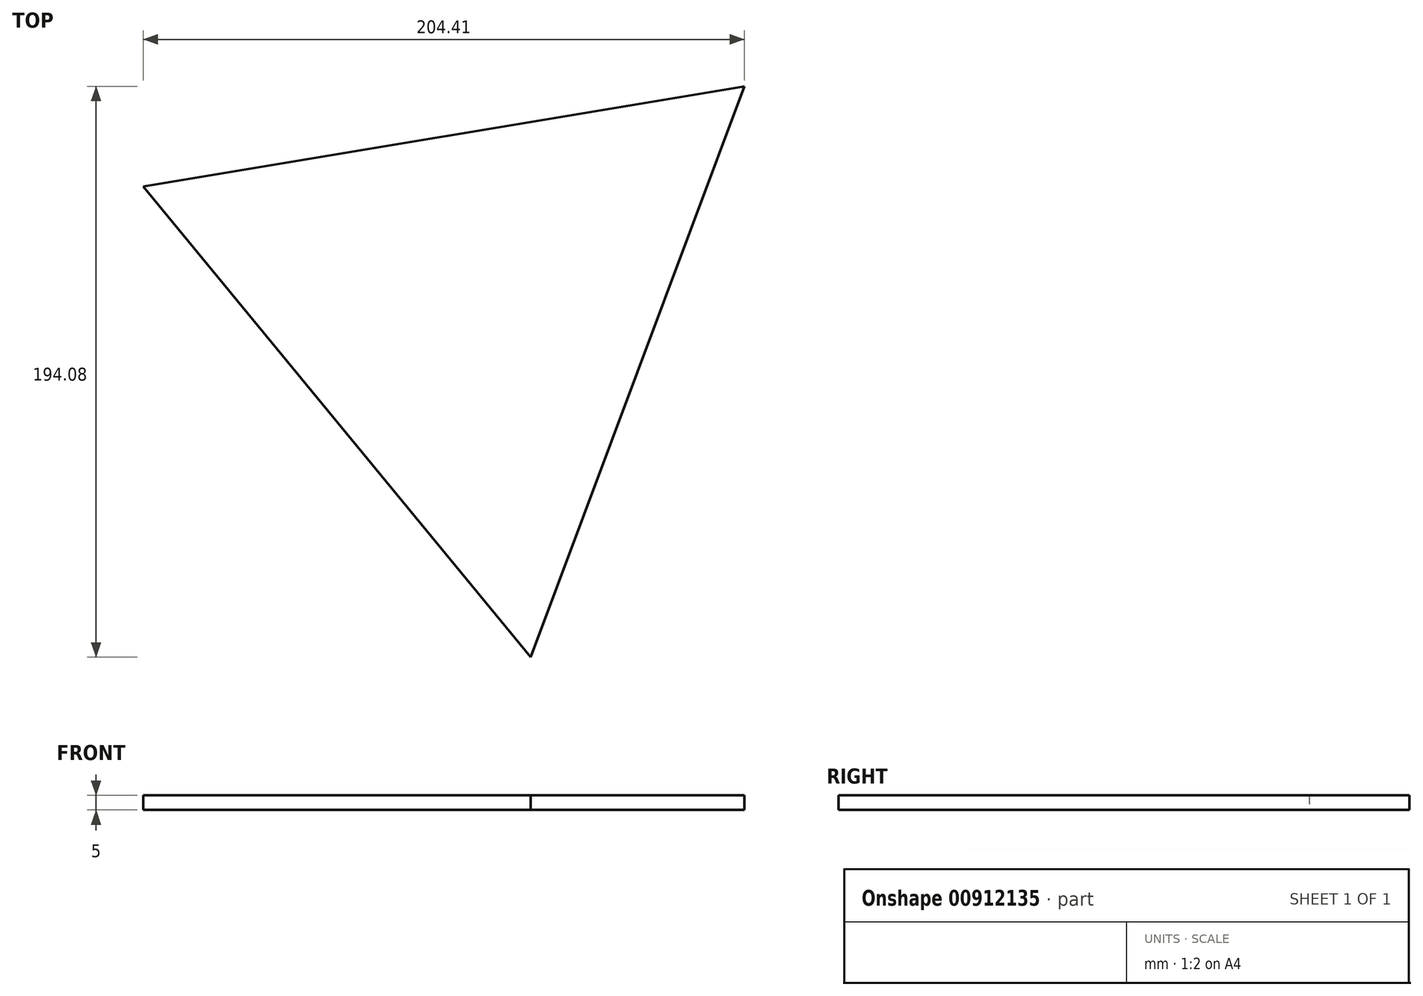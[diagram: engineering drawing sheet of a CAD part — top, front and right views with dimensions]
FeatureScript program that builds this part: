
annotation { "Feature Type Name" : "Feature", "Feature Type Description" : "" }
export const myFeature = defineFeature(function(context is Context, id is Id, definition is map)
    precondition{}
    {
        {
            var Q0;
            Q0=qCreatedBy(makeId("Top.planeOp"),FACE);
            var sketch = newSketch(context, id + "F0", { "sketchPlane" : qUnion([Q0])});
            skCircle(sketch, "E0.cCircle", {"center": v(-8.62, 59.4) * mm, "radius": 59.82 * mm, "construction": true});
            skLineSegment(sketch, "E0.0", {"start": v(83.74, 135.47) * mm, "end": v(11.07, -58.6) * mm});
            skLineSegment(sketch, "E0.1", {"start": v(11.07, -58.6) * mm, "end": v(-120.67, 101.36) * mm});
            skLineSegment(sketch, "E0.2", {"start": v(-120.67, 101.36) * mm, "end": v(83.74, 135.47) * mm});
            skPoint(sketch, "E0.0.midPoint", {"position": v(47.4, 38.43) * mm});
            skSolve(sketch);
        }
        {
            var Q0;
            Q0=makeQuery(id+"F0.imprint","IMPRINT",FACE,{"disambiguationData":[TD([[makeQuery(id+"F0.imprint","IMPRINT",EDGE,{"derivedFrom":sQuery(id+"F0.wireOp",EDGE,"E0.0")}),-1.0]])]});
            extrude(context, id + "F1", {"entities" : qUnion([Q0]), "depth" : 5 * mm, "offsetDistance" : 25.4 * mm});
        }
    });
